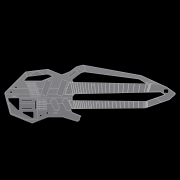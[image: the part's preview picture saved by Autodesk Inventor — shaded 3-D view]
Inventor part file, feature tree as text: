
AUTODESK INVENTOR PART (.ipt)
format: ipt  version: 2020 (Build 240168000, 168)  size: 9,611,776 bytes
history: native  units: in
note: dims shown in document units (in); Inventor stores cm internally (conversion verified against a paired STEP export)
features: other x165, extrude x70, fillet x51, projected_geometry x6, sketch x5, hole x4, loft x3, reference x2, plane x1, move_body x1
ambient origin geometry x8: Origin, YZ Plane, XZ Plane, XY Plane, X Axis, Y Axis, Z Axis, Center Point
bodies: Body (feature_tree), BodyFeature (feature_tree), BodyCut (feature_tree), BodyCutFeature (feature_tree), BodyCutFilletFeature (feature_tree), BodyCutCombineFeature (feature_tree), BodyCutEdgeFilletFeature (feature_tree), BodyRibFrontFilletsFeature (feature_tree), BodyBackRibFilletsFeature (feature_tree), BodyFretboardFilletsFeature (feature_tree), BodyFrontTopFilletsFeature (feature_tree), BodyFrontBottomFilletsFeature (feature_tree), BodyFrontNeckFilletsFeature (feature_tree), Solid22 (feature_tree), Solid23 (feature_tree), Solid62 (feature_tree), Solid64 (feature_tree), Solid65 (feature_tree), Solid68 (feature_tree), Solid50 (feature_tree), Solid52 (feature_tree), Solid54 (feature_tree), Solid56 (feature_tree), Solid57 (feature_tree), Solid59 (feature_tree)
feature tree (308):
  other  "MainBody"
  extrude  "NeckMountsProfileFeature"  Depth=0.5in TaperAngle=0.0deg
  other  "NeckPlane"
  extrude  "8StringFeature"  Depth=4.5in
  extrude  "6StringFeature"  Depth=1.12in
  extrude  "HornFeature"  Depth=0.6788in
  other  "6StringNeckFeature"
  other  "8StringNeckFeature"
  fillet  "InsideCornerFilletsFeature1/8"  Radius=0.6788in
  fillet  "OutsideFilletsFeature1/2"  Radius=0.125in
  fillet  "NeckMountOutsideFilletsFeature1/4"  Radius=0.5in
  fillet  "TipFilletsFeature1/8"  Radius=0.125in
  fillet  "BottomHornTipFilletFeature1/10"  Radius=0.1in
  fillet  "BottomHornFilletsFeature1/8"  Radius=0.125in
  fillet  "InsideHandleFilletsFeature1/2"  Radius=0.5in
  fillet  "InsideHandleFilletsFeature1/8"  Radius=0.125in
  fillet  "InsideTopHornFilletsFeature1/4"  Radius=0.25in
  fillet  "InsideTopHornFilletsFeature1/2"  Radius=0.5in
  fillet  "InsideBottomHornFilletsFeature1/4"  Radius=0.25in
  other  "PickupsOriginal"
  other  "MiddlePlane"
  other  "PickupsCustom"
  other  "PickupsModified"
  extrude  "TopPickupsIndentFeature"  Depth=0.05in
  extrude  "BottomPickupsIndentFeature"  Depth=0.05in
  extrude  "TopPickupHolesFeature"  Depth=0.05in
  extrude  "BottomPickupHolesFeature"  Depth=0.05in
  fillet  "PickupIndentFilletsFeature"  Radius=1.1649in
  other  "Frets"
  other  "FretsPreview"
  other  "TopHornHandleIndent"
  extrude  "TopHornBodyHandleFeature"  Depth=0.05in
  extrude  "TopHornHornHandleFeature"  Depth=0.05in
  other  "HornSculptFeature"
  other  "TopHornHandleFront"
  extrude  "TopHornHandleFrontFeature"  Depth=0.05in
  extrude  "TopHornHandleFront2Feature"  Depth=0.05in
  extrude  "TopHornHandleFront3Feature"  TaperAngle=45.0deg  [1 undecoded]
  other  "TopHornHandleBack"
  extrude  "TopHornHandleBackFeature"  TaperAngle=120.0deg  [1 undecoded]
  extrude  "TopHornHandleBack2Feature"  Depth=0.05in
  extrude  "TopHandleFeature"  Depth=0.05in
  extrude  "TopHandleFrontFeature"  Depth=0.05in
  extrude  "TopHandleBackFeature"  Depth=0.05in
  other  "Tuners"
  hole  "TunerHolesFeature"  [1 undecoded]
  other  "LogoMount"
  extrude  "LogoMountFeature"  Depth=0.05in
  other  "SideProfile"
  extrude  "SideProfileFeature"  Depth=0.05in
  other  "KeyboardCompartmentSidePlane"
  extrude  "KeyboardCompartmentFeature"  Depth=0.05in
  fillet  "KeyboardCompartmentFilletsFeature"  Radius=0.101in
  other  "ControlsBottom"
  other  "ControlsTop2"
  other  "ControlsTop1"
  extrude  "ControlsTop1Feature"  Depth=0.05in
  extrude  "ControlsTop2Feature"  Depth=0.05in
  extrude  "ControlsBottomFeature"  Depth=0.05in
  other  "HornSculptSideProfileFeature"
  fillet  "HornFretboardFilletFeature"  Radius=0.933in
  other  "ElectronicsCompartments"
  other  "InsideFacePlane1"
  other  "InsideFacePlane2"
  other  "InsideFacePlane3"
  extrude  "ElectronicCompartmentTopFeature"  Depth=0.05in
  extrude  "ElectronicCompartmentBottomFeature"  Depth=0.05in
  other  "ElectronicCompartmentsSculpt1Feature"
  other  "ElectronicCompartmentsSculpt2Feature"
  other  "ElectronicCompartmentsSculpt3Feature"
  other  "ElectronicCompartmentsSubtractFeature"
  extrude  "ElectronicCompartmentsSubtract2Feature"  Depth=0.05in
  fillet  "ElectronicCompartmentFillets1Feature"  Radius=3.5in
  fillet  "ElectronicCompartmentFillets2Feature"  Radius=1.277in
  extrude  "ControlIndentsBottomFeature"  Depth=0.05in
  fillet  "ElectronicCompartmentFillets3Feature"  Radius=1.5in
  fillet  "ElectronicCompartmentFillets4Feature"  Radius=1.0857in
  extrude  "ControlIndentsTopFeature"  Depth=0.05in
  other  "ControlIndents2Top"
  extrude  "ControlIndents2TopFeature"  Depth=0.05in
  fillet  "ControlIndents3FilletsFeature"  Radius=4.5in
  extrude  "ControlIndents2RecutFeature"  Depth=0.05in
  fillet  "ElectronicCompartmentInsideFilletsFeature"  Radius=0.1512in
  other  "BottomBridgePickupWirePlane"
  extrude  "BottomBridgePickupWireHoleFeature"  Depth=0.05in
  other  "BottomNeckPickupWirePlane"
  extrude  "BottomNeckPickupWireFeature"  Depth=0.05in
  extrude  "TopPickupWireFeature"  Depth=0.05in
  other  "SeaboardBlockCircuitboardMounts"
  extrude  "SeaboardBlockMountStemFeature"  Depth=0.05in
  extrude  "SeaboardBlockMountsFeature"  Depth=0.05in
  other  "SeaboardBlockKeyMounts"
  extrude  "SeaboardBlockKeyMountsFeature"  Depth=0.05in
  extrude  "SeaboardBlockRibbonsFeature"  Depth=0.05in
  extrude  "TunersTopFeature"  Depth=0.05in
  extrude  "TunersMiddleFeature"  Depth=0.05in
  extrude  "TunersBottomFeature"  Depth=0.05in
  fillet  "TunerFilletsFeature"  Radius=1.1386in
  extrude  "NeckCutFeature"  Depth=0.05in
  fillet  "NeckCutFilletFeature"  Radius=4.009in
  other  "NeckCutCombineFeature"
  fillet  "NeckCutEdgeFilletFeature"  Radius=1.481in
  fillet  "NeckCutCornerFilletsFeature"  Radius=0.25in
  extrude  "NeckMountsFeature"  Depth=0.05in
  extrude  "FretMarkersTopFeature"  Depth=0.05in
  extrude  "FretMarkersBottomFeature"  Depth=0.05in
  extrude  "FretsPreviewFeature"  TaperAngle=0.0deg  [1 undecoded]
  extrude  "FretLocksPreviewFeature"  Depth=0.3937in
  hole  "FretLocksHolesFeature"  [1 undecoded]
  extrude  "TopHornHandleBodyFeature"  Depth=0.05in
  other  "TopHornSculpt3Feature"
  other  "TopHornSculpt4Feature"
  other  "TopHornSculpt5Feature"
  fillet  "TopHornHandleBodyFilletsFeature"  Radius=0.9256in
  fillet  "TopHornHandleFilletsFeature"  [1 undecoded]
  other  "TopHornAdjustFeature"
  fillet  "TopHornAdjustFilletFeature"  [1 undecoded]
  other  "HandlePlane1"
  other  "HandlePlane2"
  other  "Handle"
  extrude  "HandleBackFeature"  Depth=0.05in
  extrude  "HandleFrontFeature"  Depth=0.05in
  other  "HandleSculpt1Feature"
  other  "HandleSculpt2Feature"
  other  "HandleSculpt3Feature"
  other  "HandleSculpt4Feature"
  other  "HandleSculpt5Feature"
  other  "HandleSculpt6Feature"
  other  "HandleEdit1Feature"
  other  "HandleEdit2Feature"
  fillet  "HandleBodyFilletsFeature"  Radius=25.5in
  fillet  "HandleRibFilletsFeature"  Radius=0.3333in
  other  "HornBackSculptFeature"
  other  "HornHandleBackSculpt1Feature"
  other  "HornHandleBackSculpt2Feature"
  fillet  "HornHandleackSculptFilletsFeature"  Radius=0.333in
  fillet  "HandleMeshFilletsFeature"  Radius=0.1in
  fillet  "HornMeshFillets1Feature"  Radius=0.1in
  fillet  "FretboardEndFilletsFeature"  [1 undecoded]
  other  "KeyboardCompartmentSideProfile"
  extrude  "KeyboardCompartmentExactFeature"  Depth=0.05in
  extrude  "KeyboardCompartmentSideFeature"  Depth=0.05in
  other  "KeyboardCompartmentExactSubtractFeature"
  other  "8NeckSplitFeature"
  other  "8NeckLoftStartPlane"
  other  "8NeckLoftEndPlane"
  loft  "8NeckLoftFeature"
  other  "6NeckSplitForLoftFeature"
  other  "6NeckLoftEndPlane"
  other  "6NeckLoftStartPlane"
  extrude  "OscScreenFeature"  TaperAngle=0.0deg  [1 undecoded]
  other  "OscCompartmentPlane"
  other  "OscIndentPlane"
  extrude  "OscCompartmentFeature"  Depth=0.05in
  other  "OscCompartmentSubtractFeature"
  extrude  "OscMountFeature"  Depth=0.05in
  other  "OscCoverIndentPlane"
  extrude  "OscCoverIndentFeature"  Depth=0.05in
  fillet  "OscCoverIndentFilletsFeature"  [1 undecoded]
  extrude  "OscCoverMountHolesFeature"  Depth=0.05in TaperAngle=0.0deg
  fillet  "ElectronicCompartmentLastFilletFeature"  Radius=0.3in
  loft  "6NeckLoftFeature"
  extrude  "6CloseCutFeature"  Depth=0.05in
  other  "HeadSculpt1Feature"
  other  "HeadThickness"
  other  "HeadSculpt2Feature"
  other  "HeadSculpt3Plane"
  extrude  "HeadSculpt3Feature"  Depth=0.05in
  other  "HeadSculpt4Feature"
  other  "8HeadCombineFeature"
  other  "8HeadCleanupFeature"
  fillet  "8HeadFilletFeature"  Radius=0.333in
  other  "HeadSculpt5Plane"
  other  "HeadSculpt5Feature"
  other  "HeadSculpt6Feature"
  other  "HeadSculpt7Plane"
  extrude  "HeadSculpt7Feature"  Depth=0.05in
  other  "6StringCombineFeature"
  other  "6NeckFilletSplitFeature"
  other  "8NeckFilletSplitFeature"
  fillet  "InsideHeadFilletFeature"  Radius=0.125in
  other  "CombineFilletsFeature"
  fillet  "HornHeadFilletsFeature"  Radius=0.5in
  fillet  "HornFillet3Feature"  Radius=5.55in
  other  "HornFinalSplitFeature"
  other  "6FinalSplitFeature"
  other  "6CombineFeature"
  other  "8NeckJoin"
  other  "6NeckJoin"
  extrude  "8NeckJoinFeature"  Depth=0.05in
  fillet  "8NeckJoinFilletFeature"  Radius=0.2in
  extrude  "6NeckJoinFeature"  Depth=0.05in
  extrude  "SeaboardBlockMountHolesFeature"  TaperAngle=0.0deg  [1 undecoded]
  extrude  "PickupRecutFeature"  Depth=0.05in
  extrude  "BackCoverIndentFeature"  Depth=0.3937in
  extrude  "ElectronicsCompartmentSupportFeature"  Depth=0.05in
  fillet  "ElectronicsCompartmentSupportFilletsFeature"  Radius=1.125in
  hole  "BackCoverMountsFeature"  [1 undecoded]
  other  "OscCoverBottom"
  other  "OscCoverTopPlane"
  other  "OscCoverMounts"
  loft  "OscCoverFeature"
  extrude  "OscCoverBodyCutFeature"  Depth=0.05in TaperAngle=0.0deg
  fillet  "OscCoverBodyCutFilletsFeature"  Radius=0.05in
  other  "OscCoverBodyCutSubtractFeature"
  fillet  "OscCoverBodyFilletFeature"  Radius=0.125in
  extrude  "OscCoverMountsFeature"  Depth=0.05in
  other  "LogoCompartment"
  extrude  "LogoCompartmentFeature"  Depth=0.05in
  extrude  "LogoCompartmentMountsFeature"  Depth=0.05in
  fillet  "LogoCompartmentFillet1Feature"  Radius=0.5in
  fillet  "LogoCompartmentFillet2Feature"  Radius=0.25in
  fillet  "LogoCompartmentFillet3Feature"  Radius=0.1in
  fillet  "LogoCompartmentFillet4Feature"  Radius=0.13in
  fillet  "LogoCompartmentFillet5Feature"  Radius=3.063in
  fillet  "LogoCompartmentFillet6Feature"  Radius=0.1295in
  fillet  "LogoCompartmentFillet7Feature"  Radius=0.1295in
  fillet  "LogoCompartmentFillet8Feature"  Radius=0.5708in
  hole  "LogoCompartmentHolesFeature"  [1 undecoded]
  other  "KeyboardCompartment"
  other  "TopHandle"
  other  "TunerLocksBody"
  other  "FretsBody"
  other  "TunersTop"
  other  "TunersMiddle"
  other  "TunersBottom"
  other  "ElectronicCompartments1Body"
  other  "NeckCut"
  other  "NeckMounts"
  other  "TopHornHandle"
  other  "TopHornHandleBody"
  projected_geometry  "Projected Loop22"
  projected_geometry  "Projected Loop23"
  other  "TopHandleFront"
  projected_geometry  "Projected Loop24"
  other  "TopHandleBack"
  other  "HandleBody"
  other  "TopHornSculpt3Plane"
  other  "TopHornSculpt4Plane"
  other  "TopHornSculpt5Plane"
  other  "HandleSculpt1Plane"
  other  "HandleSculpt2Plane"
  other  "HandleSculpt3Plane"
  other  "HandleSculpt4Plane"
  other  "HandleSculpt5Plane"
  other  "HandleSculpt6Plane"
  other  "HornBody"
  other  "8StringBody"
  other  "6StringBody"
  other  "NeckMountsProfile"
  other  "HornBackSculptPlane"
  other  "HornSculptFrontPlane"
  plane  "Work Plane62"
  other  "8NeckStartProfile"
  other  "8NeckEndProfile"
  sketch  "Sketch127"  dims[d8=0.7696in d18=0.5in d119=1.75in d120=0.0in]
  other  "6NeckLoftStartProfile"
  other  "6NeckLoftEndProfile"
  projected_geometry  "Projected Loop27"
  other  "6CloseCut"
  sketch  "Sketch131"  dims[d433=1.0857in d464=4.5in d466=0.25in]
  other  "HeadSculpt1Plane"
  other  "HeadSculpt2Plane"
  other  "HeadSculpt3Profile"
  other  "HeadSculpt4Plane"
  other  "HeadSculpt7Profile"
  other  "6NeckFilletSplit"
  other  "8NeckFilletSplit"
  sketch  "Sketch138"  dims[d501=0.25in d582=1.12in]
  sketch  "Sketch139"  dims[d644=25.0in d654=0.6788in d681=0.6788in d700=0.125in d702=0.5in d703=0.125in d705=0.1in d706=0.125in d707=0.5in d708=0.125in d709=0.25in d710=0.5in d711=0.25in]
  other  "ControlIndentsBottom"
  other  "BottomBridgePickupWireHole"
  other  "BottomNeckPickupWire"
  other  "TopPickupWire"
  other  "HornHandleBackSculpt1Plane"
  other  "HornHandleBackSculpt2Plane"
  sketch  "Sketch165"  dims[d716=2.2835in d717=0.0515in d718=13.825in d719=0.213in d721=0.9414in d722=1.1649in d724=5.7in d725=7.5379in d726=0.2542in d727=2.0in d728=45.0deg d729=120.0deg d730=0.3642in d731=0.9371in d745=5.6289in d747=6.0in d748=4.3in d750=0.8658in d751=0.6506in d753=0.4054in d754=0.8in d779=0.101in d781=1.7in d782=7.125in d783=2.6in d784=0.933in d787=1.1in d792=3.625in d793=4.0in d819=3.5in d825=1.277in d834=1.277in d836=1.5in d837=1.0857in d838=3.0in d839=2.0in d841=4.5in d846=3.3665in d850=0.1512in d853=2.6in d864=1.5757in d961=0.5in d962=0.5in d963=0.3779in d964=0.3779in d965=0.45in d966=0.45in d967=0.8795in d968=1.1386in d969=1.1386in d970=0.45in d971=4.009in d972=1.481in d979=0.25in d980=0.25in d982=0.1718in d983=0.1718in d984=0.0in d985=0.7874in d987=4.0in d988=0.3937in d990=1.0in d994=2.746in d995=1.481in d996=0.9256in d999=0.0in d1000=0.0in d1022=26.75in d1023=28.0in d1024=25.5in d1026=0.3333in d1041=0.333in d1042=0.1in d1044=0.1in d1048=0.0in d1049=0.0in d1054=0.1in d1055=0.1in d1057=0.748in d1060=0.0in d1061=0.0in d1064=0.4662in d1092=0.7in d1095=1.7in d1100=0.0in d1101=0.0in d1117=0.25in d1118=0.0in d1119=0.3in d1120=0.0in d1122=0.2in d1123=0.0in d1277=0.6459in d1329=0.5333in d1334=0.333in d1335=0.5333in d1339=0.125in d1348=0.5in d1358=5.55in d1359=1.75in d1373=0.2in d1375=0.1in d1376=0.0in d1406=1.125in d1430=3.1496in d1432=0.525in d1433=0.3937in d1435=1.0in d1439=1.8in d1440=1.125in d1441=0.2in d1475=0.1in d1476=0.75in d1477=0.375in d1478=0.25in d1479=0.5635in d1480=0.5in d1481=0.8108in d1483=0.05in d1484=0.0in d1485=0.05in d1486=0.0in d1487=0.05in d1488=0.0in d1489=0.125in d1490=0.1in d1491=2.846in d1492=1.481in d1493=0.5in d1494=0.25in d1496=0.1in d1504=0.13in d1508=0.1in d1511=3.063in d1512=0.1295in d1513=0.1295in d1526=0.5708in d1527=0.1286in d1528=1.3799in d1529=1.3958in d1530=1.1055in d1531=0.8208in d1534=2.3622in d1536=0.45in d1537=0.3937in d1539=1.0in d1574=1.0in d1575=0.0in d1576=0.0in d1577=0.4789in d1578=0.4308in d1579=1.1471in d1580=2.5in d1581=1.275in d1582=1.1845in d1583=1.481in d1584=1.1384in d1585=0.7644in d1586=2.746in d1587=0.264in d1588=0.4in d1589=0.0in d1590=0.75in d1591=0.0in d1592=1.0in d1593=0.0in d1594=1.0in d1595=0.0in d1596=0.144in d1597=3.75in d1598=0.1295in d1599=0.1295in d1638=10.0in d1639=14.2465in d1641=11.25in d1648=0.5in d1649=0.0in d1650=28.0in d1657=1.0in d1659=5.5in d1660=4.25in d1662=0.3333in d1663=0.0in d1664=10.0in d1665=1.0in d1671=0.1in d1672=0.5in d1676=3.0in d1677=2.425in d1682=0.75in d1683=0.0in d1690=1.1878in d1691=0.9817in d1692=1.0844in d1693=0.8784in d1695=0.2in d1696=0.0in d1750=1.525in d1751=0.0in d1752=0.5in d1777=0.5in d1778=0.0in d1779=0.5in d1780=0.0in d1781=0.5in d1782=0.0in d1783=0.6in d1784=0.0in d1790=0.65in d1791=0.0in d1792=0.65in d1793=0.0in d1795=0.125in d1821=0.1in d1828=0.0in d1829=0.0in d1830=0.475in d1831=0.125in d1832=0.125in d1843=3.0403in d1844=2.1333in d1845=0.758in d1847=1.75in d1848=0.0in d1849=1.9in d1850=0.0in d1851=1.9in d1852=0.0in d1858=0.9in d1859=0.0in d1862=0.0in d1863=0.0in d1864=0.5in d1865=0.0in d1866=0.5in d1867=0.0in d1870=0.2056in d1871=0.257in d1872=0.0674in d1875=0.25in d1876=0.0in d1877=0.15in d1880=0.15in d1882=0.05in d1883=0.05in d1885=1.3537in d1887=10.0in d1888=0.1in d1889=0.1in d1890=20.0in d1891=20.0in d1894=0.0618in d1900=0.1in d1901=0.4524in d1903=0.006in d1904=0.0in d1915=0.22in d1921=0.0in d1922=90.0deg d1923=0.0in d1924=90.0deg d1925=1.2in d1926=0.7in d1927=0.3333in d1928=0.001in d1929=0.25in d1930=1.25in d1931=0.25in d1935=0.8in d1936=0.3489in d1937=0.22in d1938=0.25in d1939=0.5in d1940=0.6in d1941=0.15in d1942=0.4in d1943=0.0in d1944=90.0deg d1945=0.0in d1946=90.0deg d1948=1.3333in d1949=2.125in d1951=1.125in d1952=2.55in d1957=3.0in d1958=0.1in d1959=0.1in d1960=0.1in d1961=1.0in d1962=0.0in d1966=1.0in d1967=0.0in d1968=0.44in d1969=0.0in d1975=0.1in d1976=0.1in d1980=10.6875in d1981=5.1875in d1982=0.85in d1983=0.3333in d1985=7.5816in d1987=0.1in d1988=0.0in d1989=0.1875in d1990=0.5333in d1992=150.0deg d1993=3.25in d1996=-0.325in d1997=-0.125in d1998=1.0in d1999=0.0in d2004=0.5in d2005=0.0in d2007=0.0938in d2008=0.5in d2009=0.25in d2010=2.3125in d2011=0.7188in d2015=0.25in d2016=5.0in d2019=0.125in d2020=0.25in d2027=0.2in d2028=0.0in d2029=0.02in d2030=0.0in d2039=0.55in d2047=0.25in d2048=0.25in d2049=0.0in d2050=0.0in d2052=2.295in d2053=0.0in d2056=0.25in d2058=0.25in d2059=0.3333in d2060=0.3333in d2061=0.25in d2062=0.3333in d2063=0.3333in d2064=0.0in d2065=0.0in d2066=0.339in d2067=0.1643in d2068=0.1in d2069=0.1in d2070=0.1in d2071=0.1in d2072=0.1643in d2073=0.1643in d2074=0.1643in d2077=3.3125in d2078=3.313in d2079=0.305in d2080=0.3333in d2081=1.0in d2082=0.0in d2083=0.3333in d2084=0.0in d2086=0.719in d2087=2.3125in d2088=0.125in d2089=0.1in d2090=0.438in d2091=0.438in d2092=0.438in d2093=0.438in d2094=0.25in d2095=0.0in d2096=0.25in d2097=0.25in d2098=2.0in d2100=2.5in d2102=0.75in d2103=0.25in d2104=0.25in d2105=0.0in d2106=0.625in d2111=10.0in d2112=0.125in d2113=0.3333in d2117=1.75in d2118=1.25in d2119=1.625in d2120=0.25in d2121=1.0in d2122=0.1in d2125=0.7in d2132=1.625in d2133=1.0in d2134=0.1in d2135=1.0in d2136=1.0in d2137=0.1in d2138=1.025in d2139=1.025in d2140=0.5in d2141=0.7in d2142=1.075in d2143=0.7in d2144=0.5in d2146=0.25in d2147=0.25in d2148=0.5in d2149=1.75in d2150=0.0in d2151=0.0in d2152=0.035in d2153=0.0in d2154=0.0in d2155=0.0in d2156=-0.325in d2157=1.0in d2158=0.2in d2159=0.0in d2160=1.0in d2161=0.2in d2162=0.0in d2164=1.0in d2165=2.2612in d2166=0.605in d2167=0.01in d2168=0.3333in d2169=0.5388in d2170=0.4in d2171=2.625in d2172=1.375in d2173=0.172in d2174=0.281in d2175=0.5in d2176=0.0in d2177=-2.0in d2178=1.797in d2179=0.0in d2180=-0.125in d2181=0.06in d2182=0.06in d2183=0.505in d2184=0.9375in d2185=2.625in d2186=1.375in d2187=2.5in d2188=1.0313in d2189=0.05in d2190=0.1719in d2191=0.0625in d2192=0.0625in d2193=0.1094in d2194=0.0312in d2195=0.0312in d2196=0.0312in d2197=0.0312in d2198=0.0312in d2199=0.0312in d2200=0.0312in d2201=0.0312in d2202=0.203in d2203=0.0in d2207=-0.2in d2211=0.15in d2212=1.0in d2213=0.0in d2214=0.15in d2215=0.15in d2216=0.1in d2220=0.05in d2221=1.5in d2222=0.0in d2230=0.6836in d2238=1.0in d2239=0.25in d2240=0.1in d2241=0.0689in d2243=1.1408in d2244=0.449in d2245=1.6223in d2246=2.1038in d2247=0.449in d2248=0.0463in d2249=0.4549in d2251=0.3908in d2252=0.3908in d2255=0.8in d2257=3.5in d2259=1.1973in d2261=0.625in d2262=0.625in d2263=0.536in d2264=2.7in d2265=0.25in d2266=0.2in d2267=0.0in d2268=0.2in d2269=0.0in d2278=0.4264in d2279=1.0in d2280=0.0in d2281=21.986in d2282=0.0in d2283=0.1in d2284=0.1in d2285=0.5in d2286=0.0in d2287=0.5333in d2288=0.1in d2293=0.85in d2294=1.0in d2295=0.25in d2296=0.749in d2297=0.0in d2298=0.25in d2299=0.1984in d2300=0.1in d2301=0.0in d2302=0.2in d2303=0.0in d2304=0.481in d2305=0.481in d2306=0.5in d2307=0.25in d2308=0.1in d2309=0.75in d2310=0.375in d2311=0.25in d2312=0.5635in d2313=0.5in d2314=0.8108in d2319=0.0in d2320=0.0in d2321=90.0deg d2322=0.0in d2323=90.0deg d2324=0.5in d2325=0.0in d2326=28.0in d2327=1.0in d2328=1.5in d2329=0.0in d2330=0.2in d2331=0.2in d2333=0.22in d2335=0.12in d2336=0.12in d2337=0.1in d2338=0.1in d2339=0.75in d2340=0.375in d2341=0.25in d2342=0.5635in d2343=0.5in d2344=0.8108in d2347=0.25in d2348=0.3in d2349=0.15in d2350=0.15in d2351=0.3in d2352=0.15in d2353=0.3in d2354=0.25in d2355=0.25in d2356=0.25in d2357=0.25in d2358=0.25in d2359=0.1958in d2360=0.1958in d2365=0.2in d2366=0.0in d2381=0.7in d2382=0.6in d2387=0.089in d2408=0.3333in d2409=0.0in d2410=0.031in d2412=0.106in d2413=0.072in d2414=0.033in d2415=0.125in d2416=0.132in d2417=0.101in d2418=0.074in d2419=0.05in d2420=0.75in d2421=0.375in d2422=0.25in d2423=0.5635in d2424=0.5in d2425=0.8108in d620=0.5in d621=0.0344in d622=0.5in d623=0.0344in d1625=0.5in d1626=0.0344in d1627=0.5in d1628=0.0344in d1730=0.5in d1731=0.0344in d1732=0.5in d1733=0.0344in d1822=0.5in d1823=0.0344in d1824=0.5in d1825=0.0344in d1837=0.5in d1838=0.0344in d1839=0.5in d1840=0.0344in d1860=0.5in d1861=0.0344in d1947=0.5in d1950=0.0344in d2012=0.5in d2013=0.0344in d2101=0.5in d2392=0.5in d2393=0.0344in d2394=0.5in d2395=0.0344in]
  other  "OscScreen"
  other  "OscCompartment"
  other  "OscMount"
  other  "OscCoverPlane"
  other  "OscCoverIndent"
  other  "OscCoverMountHoles"
  projected_geometry  "Projected Loop32"
  other  "KeyboardCompartmentExact"
  projected_geometry  "Projected Loop35"
  other  "SeaboardBlockMountHoles"
  reference  "Reference6"
  reference  "Reference7"
  other  "PickupRecut"
  other  "BackCoverIndent"
  other  "ElectronicsCompartmentSupport"
  other  "BackCoverMounts"
  other  "OscCoverTop"
  other  "OscCoverBody"
  other  "Delete13"
  move_body  "Move3"
  other  "Delete14"
  other  "6StringNeckCombineBody"
  other  "8StringNeckBody"
  other  "6StringNeckBody"
  other  "TopHornBody"
  other  "8StringCombinedBody"
  other  "6StringCombinedBody"
  other  "Delete18"
  other  "<userpath>\Desktop\switchback\src\switchback-exploded.iam"
  other  "switchback-exploded.iam"
  other  "seaboard-block-keyboard:1"
note: 13 required parameter values undecoded (feature->parameter linkage not recoverable at this tier; creation-order binding heuristic only, values carry confidence <= 0.55)
